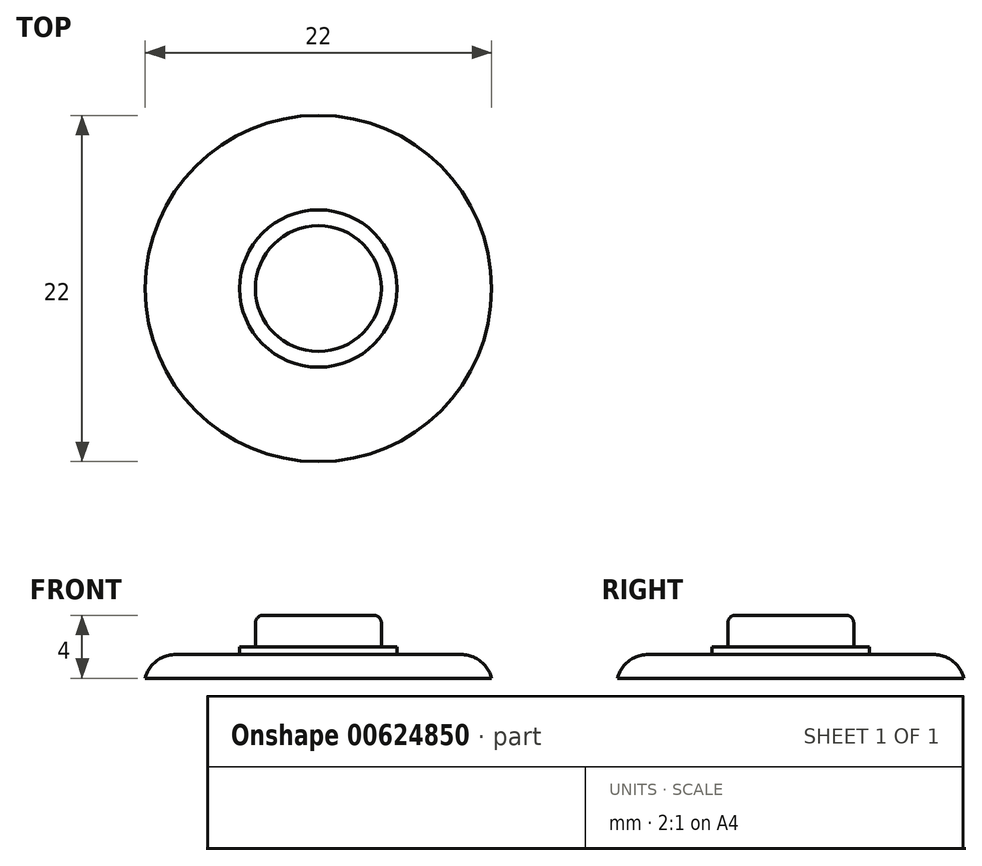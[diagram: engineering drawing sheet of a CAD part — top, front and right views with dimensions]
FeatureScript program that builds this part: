
annotation { "Feature Type Name" : "Feature", "Feature Type Description" : "" }
export const myFeature = defineFeature(function(context is Context, id is Id, definition is map)
    precondition{}
    {
        {
            var Q0;
            Q0=qCreatedBy(makeId("Top.planeOp"),FACE);
            var sketch = newSketch(context, id + "F0", { "sketchPlane" : qUnion([Q0])});
            skCircle(sketch, "E0", {"center": v(0, 0) * mm, "radius": 11 * mm});
            skSolve(sketch);
        }
        {
            var Q0;
            Q0=makeQuery(id+"F0.imprint","IMPRINT",FACE,{"disambiguationData":[TD([[makeQuery(id+"F0.imprint","IMPRINT",EDGE,{"derivedFrom":sQuery(id+"F0.wireOp",EDGE,"E0")}),1.0]])]});
            extrude(context, id + "F1", {"entities" : qUnion([Q0]), "depth" : 1.5 * mm, "offsetDistance" : 25 * mm});
        }
        {
            var Q0;
            Q0=makeQuery(id+"F1.opExtrude","CAP_FACE",FACE,{"disambiguationData":[OSD([sQuery(id+"F0.wireOp",EDGE,"E0")])],"isStart":false});
            var sketch = newSketch(context, id + "F2", { "sketchPlane" : qUnion([Q0])});
            skCircle(sketch, "E1", {"center": v(0, 0) * mm, "radius": 5 * mm});
            skSolve(sketch);
        }
        {
            var Q0;
            Q0 = qSketchRegion(id + "F2", true);
            extrude(context, id + "F3", {"entities" : qUnion([Q0]), "operationType" : NewBodyOperationType.ADD, "depth" : 0.5 * mm, "offsetDistance" : 25 * mm});
        }
        {
            var Q0;
            Q0=makeQuery(id+"F3.opExtrude","CAP_FACE",FACE,{"disambiguationData":[OSD([sQuery(id+"F2.wireOp",EDGE,"E1")])],"isStart":false});
            var sketch = newSketch(context, id + "F4", { "sketchPlane" : qUnion([Q0])});
            skCircle(sketch, "E2", {"center": v(0, 0) * mm, "radius": 4 * mm});
            skSolve(sketch);
        }
        {
            var Q0;
            Q0=makeQuery(id+"F4.imprint","IMPRINT",FACE,{"disambiguationData":[TD([[makeQuery(id+"F4.imprint","IMPRINT",EDGE,{"derivedFrom":sQuery(id+"F4.wireOp",EDGE,"E2")}),1.0]])]});
            extrude(context, id + "F5", {"entities" : qUnion([Q0]), "operationType" : NewBodyOperationType.ADD, "depth" : 2 * mm, "offsetDistance" : 25 * mm});
        }
        {
            var Q0;
            Q0=makeQuery(id+"F5.opExtrude","CAP_FACE",FACE,{"disambiguationData":[OSD([sQuery(id+"F4.wireOp",EDGE,"E2")])],"isStart":false});
            fillet(context, id + "F6", {"entities" : qUnion([Q0]), "radius" : 0.5 * mm, "tangentPropagation" : true, "allowEdgeOverflow" : false});
        }
        {
            var Q0;
            Q0=makeQuery(id+"F1.opExtrude","CAP_EDGE",EDGE,{"disambiguationData":[OSD([sQuery(id+"F0.wireOp",EDGE,"E0")])],"isStart":false});
            fillet(context, id + "F7", {"entities" : qUnion([Q0]), "radius" : 2 * mm, "tangentPropagation" : true, "allowEdgeOverflow" : false});
        }
    });
